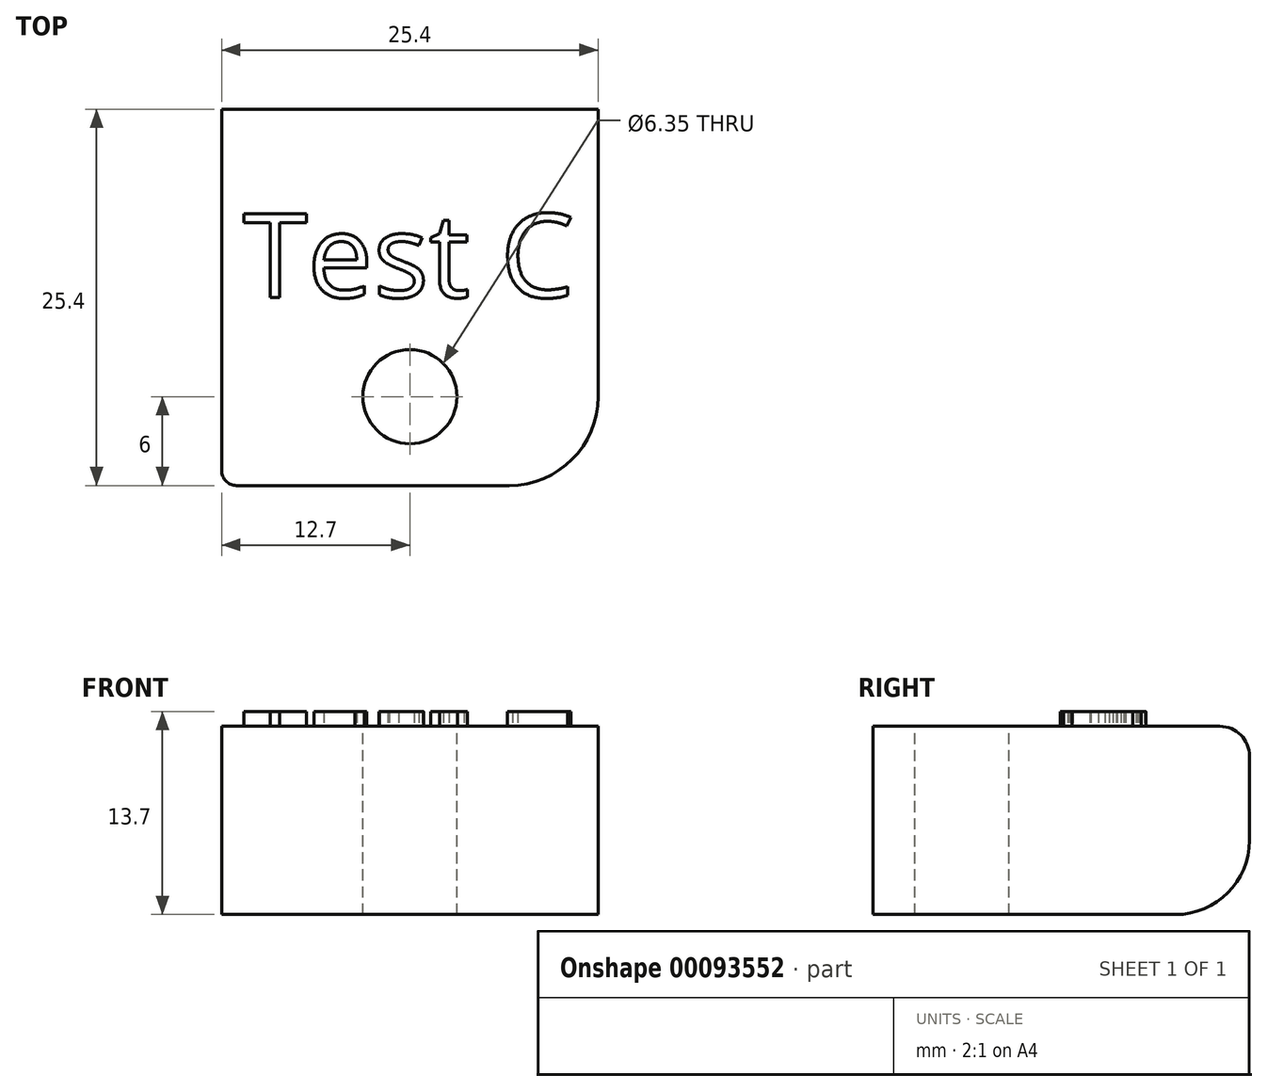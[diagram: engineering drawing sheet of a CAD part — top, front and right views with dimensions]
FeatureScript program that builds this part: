
annotation { "Feature Type Name" : "Feature", "Feature Type Description" : "" }
export const myFeature = defineFeature(function(context is Context, id is Id, definition is map)
    precondition{}
    {
        {
            var Q0;
            Q0=qCreatedBy(makeId("Top.planeOp"),FACE);
            var sketch = newSketch(context, id + "F0", { "sketchPlane" : qUnion([Q0])});
            skLineSegment(sketch, "E0.bottom", {"start": v(12.7, 12.7) * mm, "end": v(-12.7, 12.7) * mm});
            skLineSegment(sketch, "E0.top", {"start": v(12.7, -12.7) * mm, "end": v(-12.7, -12.7) * mm});
            skLineSegment(sketch, "E0.left", {"start": v(12.7, 12.7) * mm, "end": v(12.7, -12.7) * mm});
            skLineSegment(sketch, "E0.right", {"start": v(-12.7, 12.7) * mm, "end": v(-12.7, -12.7) * mm});
            skPoint(sketch, "E0.middle", {"position": v(0, 0) * mm});
            skSolve(sketch);
        }
        {
            var Q0;
            Q0=qSketchRegion(id+"F0",true);
            extrude(context, id + "F1", {"entities" : qUnion([Q0]), "depth" : 12.7 * mm});
        }
        {
            var Q0;
            Q0=makeQuery(id+"F1.opExtrude","CAP_FACE",FACE,{"disambiguationData":[OSD([sQuery(id+"F0.wireOp",EDGE,"E0.bottom"),sQuery(id+"F0.wireOp",EDGE,"E0.top"),sQuery(id+"F0.wireOp",EDGE,"E0.left"),sQuery(id+"F0.wireOp",EDGE,"E0.right")])],"isStart":false});
            var sketch = newSketch(context, id + "F2", { "sketchPlane" : qUnion([Q0])});
            skCircle(sketch, "E1", {"center": v(0, -6.7) * mm, "radius": 3.17 * mm});
            skSolve(sketch);
        }
        {
            var Q0;
            Q0=qSketchRegion(id+"F2",true);
            extrude(context, id + "F3", {"entities" : qUnion([Q0]), "operationType" : NewBodyOperationType.REMOVE, "endBound" : BoundingType.THROUGH_ALL, "oppositeDirection" : true, "depth" : 25 * mm});
        }
        {
            var Q0;
            Q0=makeQuery(id+"F1.opExtrude","SWEPT_EDGE",EDGE,{"disambiguationData":[OSD([sQuery(id+"F0.wireOp",EDGE,"E0.top"),sQuery(id+"F0.wireOp",EDGE,"E0.left")])]});
            fillet(context, id + "F4", {"entities" : qUnion([Q0]), "radius" : 6 * mm, "tangentPropagation" : true, "allowEdgeOverflow" : false});
        }
        {
            var Q0;
            Q0=makeQuery(id+"F1.opExtrude","SWEPT_EDGE",EDGE,{"disambiguationData":[OSD([sQuery(id+"F0.wireOp",EDGE,"E0.top"),sQuery(id+"F0.wireOp",EDGE,"E0.right")])]});
            fillet(context, id + "F5", {"entities" : qUnion([Q0]), "radius" : 1 * mm, "tangentPropagation" : true, "allowEdgeOverflow" : false});
        }
        {
            var Q0;
            Q0=makeQuery(id+"F1.opExtrude","CAP_EDGE",EDGE,{"disambiguationData":[OSD([sQuery(id+"F0.wireOp",EDGE,"E0.bottom")])],"isStart":false});
            fillet(context, id + "F6", {"entities" : qUnion([Q0]), "radius" : 2 * mm, "tangentPropagation" : true, "allowEdgeOverflow" : false});
        }
        {
            var Q0;
            Q0=makeQuery(id+"F1.opExtrude","CAP_EDGE",EDGE,{"disambiguationData":[OSD([sQuery(id+"F0.wireOp",EDGE,"E0.bottom")])],"isStart":true});
            fillet(context, id + "F7", {"entities" : qUnion([Q0]), "radius" : 5 * mm, "tangentPropagation" : true, "allowEdgeOverflow" : false});
        }
        {
            var Q0;
            Q0=makeQuery(id+"F1.opExtrude","CAP_FACE",FACE,{"disambiguationData":[OSD([sQuery(id+"F0.wireOp",EDGE,"E0.bottom"),sQuery(id+"F0.wireOp",EDGE,"E0.top"),sQuery(id+"F0.wireOp",EDGE,"E0.left"),sQuery(id+"F0.wireOp",EDGE,"E0.right")])],"isStart":false});
            var sketch = newSketch(context, id + "F8", { "sketchPlane" : qUnion([Q0])});
            skLineSegment(sketch, "E2", {"start": v(-12.7, 0) * mm, "end": v(12.7, 0) * mm, "construction": true});
            skText(sketch, "E3", { "text": "Test C", "fontName": "OpenSans-Regular.ttf"});
            const initialGuessF8  = {"E3": [-0.01128, 0, 1, 0, 0.00568]};
            skSetInitialGuess(sketch, initialGuessF8);
            skSolve(sketch);
        }
        {
            var Q0;
            Q0=qSketchRegion(id+"F8",true);
            extrude(context, id + "F9", {"entities" : qUnion([Q0]), "operationType" : NewBodyOperationType.ADD, "depth" : 1 * mm});
        }
    });
